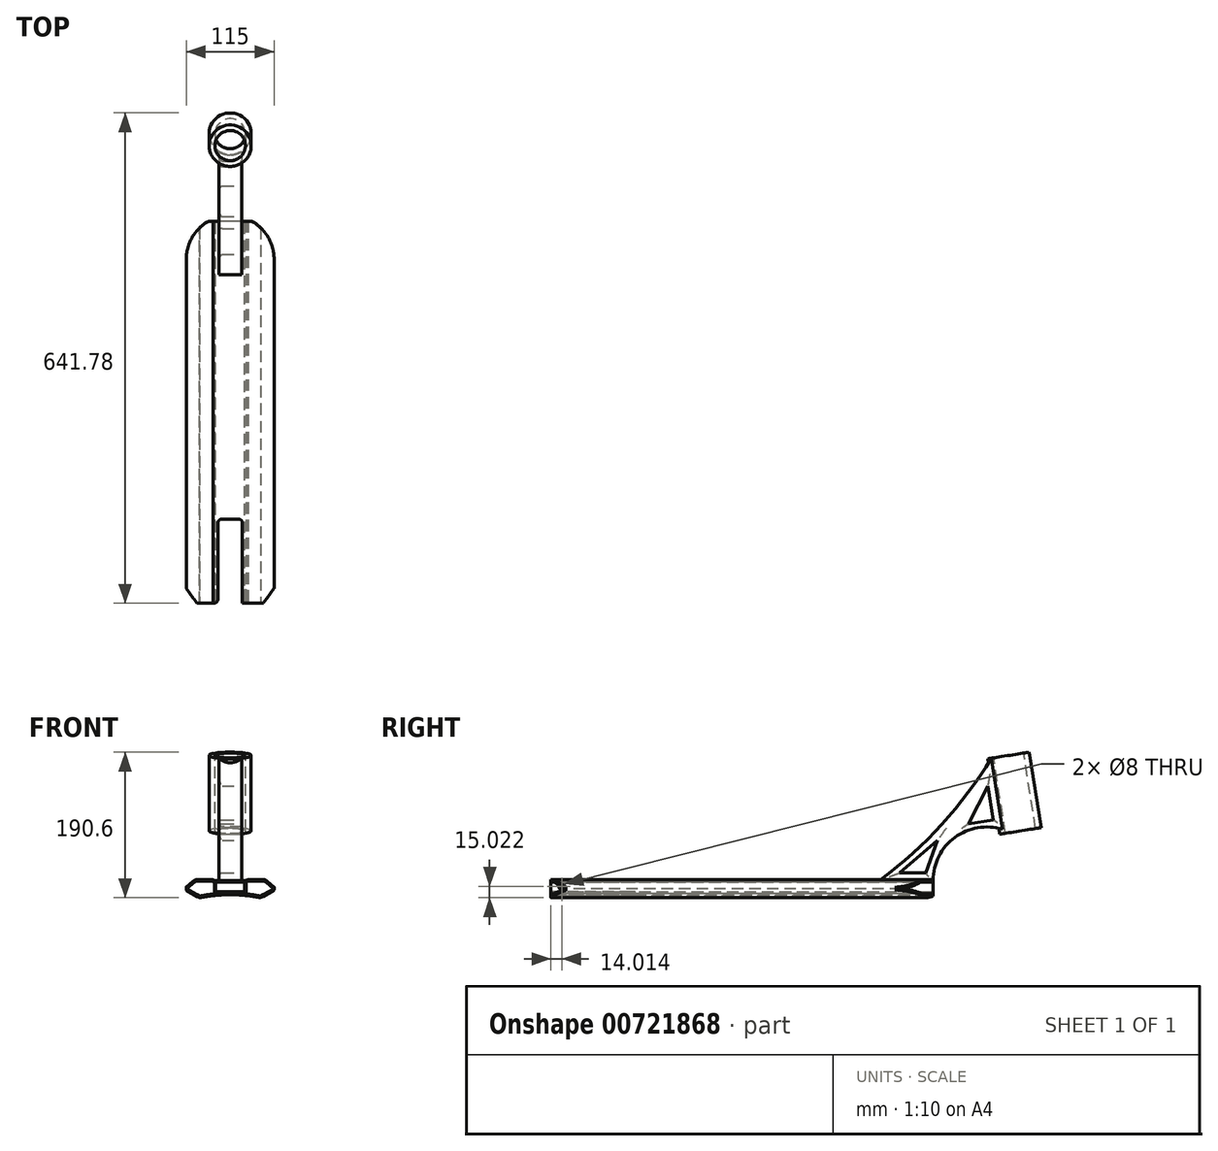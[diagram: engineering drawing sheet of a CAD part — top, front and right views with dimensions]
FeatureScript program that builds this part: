
annotation { "Feature Type Name" : "Feature", "Feature Type Description" : "" }
export const myFeature = defineFeature(function(context is Context, id is Id, definition is map)
    precondition{}
    {
        {
            var Q0;
            Q0=qCreatedBy(makeId("Front.planeOp"),FACE);
            var sketch = newSketch(context, id + "F0", { "sketchPlane" : qUnion([Q0])});
            skLineSegment(sketch, "E0", {"start": v(0, 22.7) * mm, "end": v(22.5, 22.7) * mm});
            skLineSegment(sketch, "E1", {"start": v(22.5, 22.7) * mm, "end": v(22.5, 24) * mm});
            skLineSegment(sketch, "E2", {"start": v(22.5, 24) * mm, "end": v(45.58, 24) * mm});
            skLineSegment(sketch, "E3", {"start": v(45.58, 24) * mm, "end": v(57.5, 14) * mm});
            skLineSegment(sketch, "E4", {"start": v(57.5, 14) * mm, "end": v(57.5, 10) * mm});
            skLineSegment(sketch, "E5", {"start": v(57.5, 10) * mm, "end": v(40.18, 0) * mm});
            skLineSegment(sketch, "E6.MirrorCS", {"start": v(0, 22.7) * mm, "end": v(-22.5, 22.7) * mm});
            skLineSegment(sketch, "E7.MirrorCS", {"start": v(-22.5, 22.7) * mm, "end": v(-22.5, 24) * mm});
            skLineSegment(sketch, "E8.MirrorCS", {"start": v(-22.5, 24) * mm, "end": v(-45.58, 24) * mm});
            skLineSegment(sketch, "E9.MirrorCS", {"start": v(-45.58, 24) * mm, "end": v(-57.5, 14) * mm});
            skLineSegment(sketch, "E10.MirrorCS", {"start": v(-57.5, 14) * mm, "end": v(-57.5, 10) * mm});
            skLineSegment(sketch, "E11.MirrorCS", {"start": v(-57.5, 10) * mm, "end": v(-40.18, 0) * mm});
            skArc(sketch, "E12", {"start": v(40.18, 0) * mm, "mid": v(0, 4.08) * mm, "end": v(-40.18, 0) * mm});
            skSolve(sketch);
        }
        {
            var Q0;
            Q0 = qSketchRegion(id + "F0", true);
            extrude(context, id + "F1", {"entities" : qUnion([Q0]), "endBound" : BoundingType.SYMMETRIC, "depth" : 500 * mm, "offsetDistance" : 25 * mm});
        }
        {
            var Q0;
            Q0=qCreatedBy(makeId("Front.planeOp"),FACE);
            var sketch = newSketch(context, id + "F2", { "sketchPlane" : qUnion([Q0])});
            skLineSegment(sketch, "E13.bottom", {"start": v(19, 7.7) * mm, "end": v(-19, 7.7) * mm});
            skLineSegment(sketch, "E13.top", {"start": v(19, 20.7) * mm, "end": v(-19, 20.7) * mm});
            skLineSegment(sketch, "E13.left", {"start": v(19, 7.7) * mm, "end": v(19, 20.7) * mm});
            skLineSegment(sketch, "E13.right", {"start": v(-19, 7.7) * mm, "end": v(-19, 20.7) * mm});
            skPoint(sketch, "E13.middle", {"position": v(0, 14.2) * mm});
            skSolve(sketch);
        }
        {
            var Q0;
            Q0 = qSketchRegion(id + "F2", true);
            extrude(context, id + "F3", {"entities" : qUnion([Q0]), "operationType" : NewBodyOperationType.REMOVE, "endBound" : BoundingType.SYMMETRIC, "depth" : 500 * mm, "offsetDistance" : 25 * mm});
        }
        {
            var Q0;
            Q0=makeQuery(id+"F1.opExtrude","SWEPT_EDGE",EDGE,{"disambiguationData":[OSD([sQuery(id+"F0.wireOp",EDGE,"E6.MirrorCS"),sQuery(id+"F0.wireOp",EDGE,"E7.MirrorCS")])]});
            var Q1;
            Q1=makeQuery(id+"F1.opExtrude","SWEPT_EDGE",EDGE,{"disambiguationData":[OSD([sQuery(id+"F0.wireOp",EDGE,"E0"),sQuery(id+"F0.wireOp",EDGE,"E1")])]});
            fillet(context, id + "F4", {"entities" : qUnion([Q0, Q1]), "radius" : 2 * mm, "tangentPropagation" : true, "allowEdgeOverflow" : false});
        }
        {
            var Q0;
            Q0=makeQuery(id+"F4.opFillet","BLEND_EDGE",EDGE,{"blendedFrom":[makeQuery(id+"F1.opExtrude","SWEPT_EDGE",EDGE,{"disambiguationData":[OSD([sQuery(id+"F0.wireOp",EDGE,"E0"),sQuery(id+"F0.wireOp",EDGE,"E1")])]}),makeQuery(id+"F1.opExtrude","SWEPT_FACE",FACE,{"disambiguationData":[OSD([sQuery(id+"F0.wireOp",EDGE,"E2")])]})],"blendedInto":[makeQuery(id+"F1.opExtrude","SWEPT_FACE",FACE,{"disambiguationData":[OSD([sQuery(id+"F0.wireOp",EDGE,"E2")])]})]});
            var Q1;
            Q1=makeQuery(id+"F1.opExtrude","SWEPT_EDGE",EDGE,{"disambiguationData":[OSD([sQuery(id+"F0.wireOp",EDGE,"E2"),sQuery(id+"F0.wireOp",EDGE,"E3")])]});
            var Q2;
            Q2=makeQuery(id+"F1.opExtrude","SWEPT_EDGE",EDGE,{"disambiguationData":[OSD([sQuery(id+"F0.wireOp",EDGE,"E8.MirrorCS"),sQuery(id+"F0.wireOp",EDGE,"E9.MirrorCS")])]});
            var Q3;
            Q3=makeQuery(id+"F1.opExtrude","SWEPT_EDGE",EDGE,{"disambiguationData":[OSD([sQuery(id+"F0.wireOp",EDGE,"E5"),sQuery(id+"F0.wireOp",EDGE,"E12")])]});
            fillet(context, id + "F5", {"entities" : qUnion([Q0, Q1, Q2, Q3]), "radius" : 9 * mm, "tangentPropagation" : true, "allowEdgeOverflow" : false});
        }
        {
            var Q0;
            Q0=makeQuery(id+"F1.opExtrude","SWEPT_EDGE",EDGE,{"disambiguationData":[OSD([sQuery(id+"F0.wireOp",EDGE,"E9.MirrorCS"),sQuery(id+"F0.wireOp",EDGE,"E10.MirrorCS")])]});
            var Q1;
            Q1=makeQuery(id+"F1.opExtrude","SWEPT_EDGE",EDGE,{"disambiguationData":[OSD([sQuery(id+"F0.wireOp",EDGE,"E10.MirrorCS"),sQuery(id+"F0.wireOp",EDGE,"E11.MirrorCS")])]});
            var Q2;
            Q2=makeQuery(id+"F1.opExtrude","SWEPT_EDGE",EDGE,{"disambiguationData":[OSD([sQuery(id+"F0.wireOp",EDGE,"E3"),sQuery(id+"F0.wireOp",EDGE,"E4")])]});
            var Q3;
            Q3=makeQuery(id+"F1.opExtrude","SWEPT_EDGE",EDGE,{"disambiguationData":[OSD([sQuery(id+"F0.wireOp",EDGE,"E4"),sQuery(id+"F0.wireOp",EDGE,"E5")])]});
            fillet(context, id + "F6", {"entities" : qUnion([Q0, Q1, Q2, Q3]), "radius" : 1 * mm, "tangentPropagation" : true, "allowEdgeOverflow" : false});
        }
        {
            var Q0;
            Q0=makeQuery(id+"F1.opExtrude","CAP_FACE",FACE,{"disambiguationData":[OSD([sQuery(id+"F0.wireOp",EDGE,"E0"),sQuery(id+"F0.wireOp",EDGE,"E1"),sQuery(id+"F0.wireOp",EDGE,"E2"),sQuery(id+"F0.wireOp",EDGE,"E3"),sQuery(id+"F0.wireOp",EDGE,"E4"),sQuery(id+"F0.wireOp",EDGE,"E5"),sQuery(id+"F0.wireOp",EDGE,"E6.MirrorCS"),sQuery(id+"F0.wireOp",EDGE,"E7.MirrorCS"),sQuery(id+"F0.wireOp",EDGE,"E8.MirrorCS"),sQuery(id+"F0.wireOp",EDGE,"E9.MirrorCS"),sQuery(id+"F0.wireOp",EDGE,"E10.MirrorCS"),sQuery(id+"F0.wireOp",EDGE,"E11.MirrorCS"),sQuery(id+"F0.wireOp",EDGE,"E12")])],"isStart":false});
            var sketch = newSketch(context, id + "F7", { "sketchPlane" : qUnion([Q0])});
            skArc(sketch, "E14.0", {"start": v(37.3, 2.6) * mm, "mid": v(-1.29, 6.07) * mm, "end": v(-39.84, 2.11) * mm});
            skLineSegment(sketch, "E14.1", {"start": v(-56.85, 11.93) * mm, "end": v(-39.84, 2.11) * mm});
            skArc(sketch, "E14.2", {"start": v(-20.63, 20.7) * mm, "mid": v(-22.24, 21.04) * mm, "end": v(-23.58, 22) * mm});
            skLineSegment(sketch, "E14.3", {"start": v(-23.58, 22) * mm, "end": v(-42.3, 22) * mm});
            skArc(sketch, "E14.4", {"start": v(-42.3, 22) * mm, "mid": v(-44.7, 21.58) * mm, "end": v(-46.8, 20.36) * mm});
            skLineSegment(sketch, "E14.5", {"start": v(-46.8, 20.36) * mm, "end": v(-56.85, 11.93) * mm});
            skLineSegment(sketch, "E15", {"start": v(-20.63, 20.7) * mm, "end": v(-20.63, 5.02) * mm});
            skLineSegment(sketch, "E16.MirrorCS", {"start": v(23.58, 22) * mm, "end": v(42.3, 22) * mm});
            skArc(sketch, "E17.MirrorCS", {"start": v(42.3, 22) * mm, "mid": v(44.7, 21.58) * mm, "end": v(46.8, 20.36) * mm});
            skLineSegment(sketch, "E18.MirrorCS", {"start": v(46.8, 20.36) * mm, "end": v(56.85, 11.93) * mm});
            skLineSegment(sketch, "E19.MirrorCS", {"start": v(56.85, 11.93) * mm, "end": v(39.84, 2.11) * mm});
            skArc(sketch, "E20.MirrorCS", {"start": v(-37.3, 2.6) * mm, "mid": v(1.29, 6.07) * mm, "end": v(39.84, 2.11) * mm});
            skLineSegment(sketch, "E21.MirrorCS", {"start": v(20.63, 20.7) * mm, "end": v(20.63, 5.02) * mm});
            skArc(sketch, "E22.MirrorCS", {"start": v(20.63, 20.7) * mm, "mid": v(22.24, 21.04) * mm, "end": v(23.58, 22) * mm});
            skSolve(sketch);
        }
        {
            var Q0;
            {var subQ0=sQuery(id+"F7.wireOp",EDGE,"E14.0");Q0=makeQuery(id+"F7.imprint","IMPRINT",FACE,{"disambiguationData":[TD([[makeQuery(id+"F7.imprint","IMPRINT",EDGE,{"derivedFrom":subQ0}),-1.0]])]});}
            var Q1;
            Q1=makeQuery(id+"F7.imprint","IMPRINT",FACE,{"disambiguationData":[TD([[makeQuery(id+"F7.imprint","IMPRINT",EDGE,{"derivedFrom":sQuery(id+"F7.wireOp",EDGE,"E16.MirrorCS")}),-1.0]])]});
            extrude(context, id + "F8", {"entities" : qUnion([Q0, Q1]), "operationType" : NewBodyOperationType.REMOVE, "endBound" : BoundingType.THROUGH_ALL, "oppositeDirection" : true, "depth" : 25 * mm, "offsetDistance" : 25 * mm});
        }
        {
            var Q0;
            Q0=qCreatedBy(makeId("Top.planeOp"),FACE);
            var sketch = newSketch(context, id + "F9", { "sketchPlane" : qUnion([Q0])});
            skArc(sketch, "E23", {"start": v(57.5, 200) * mm, "mid": v(0, 257.5) * mm, "end": v(-57.5, 200) * mm});
            skLineSegment(sketch, "E24", {"start": v(57.5, 200) * mm, "end": v(57.5, 280) * mm});
            skLineSegment(sketch, "E25", {"start": v(57.5, 280) * mm, "end": v(-57.5, 280) * mm});
            skLineSegment(sketch, "E26", {"start": v(-57.5, 280) * mm, "end": v(-57.5, 200) * mm});
            skSolve(sketch);
        }
        {
            var Q0;
            Q0=makeQuery(id+"F9.imprint","IMPRINT",FACE,{"disambiguationData":[TD([[makeQuery(id+"F9.imprint","IMPRINT",EDGE,{"derivedFrom":sQuery(id+"F9.wireOp",EDGE,"E23")}),-1.0]])]});
            extrude(context, id + "F10", {"entities" : qUnion([Q0]), "operationType" : NewBodyOperationType.REMOVE, "endBound" : BoundingType.THROUGH_ALL, "oppositeDirection" : true, "depth" : 25 * mm, "offsetDistance" : 25 * mm, "hasSecondDirection" : true, "secondDirectionBound" : SecondDirectionBoundingType.THROUGH_ALL, "secondDirectionOppositeDirection" : false, "secondDirectionDepth" : 25 * mm});
        }
        {
            var Q0;
            Q0=qCreatedBy(makeId("Top.planeOp"),FACE);
            var sketch = newSketch(context, id + "F11", { "sketchPlane" : qUnion([Q0])});
            skLineSegment(sketch, "E27", {"start": v(43.28, -250.03) * mm, "end": v(68, -216) * mm});
            skLineSegment(sketch, "E28", {"start": v(68, -216) * mm, "end": v(68, -346) * mm});
            skLineSegment(sketch, "E29", {"start": v(-68, -346) * mm, "end": v(-68, -216) * mm});
            skLineSegment(sketch, "E30", {"start": v(-68, -216) * mm, "end": v(-43.32, -249.97) * mm});
            skLineSegment(sketch, "E31", {"start": v(-16.12, -249.97) * mm, "end": v(-16, -139.97) * mm});
            skPoint(sketch, "E32.orphan", {"position": v(101.08, -377.14) * mm});
            skPoint(sketch, "E33.start.orphan", {"position": v(62.55, -216) * mm});
            skLineSegment(sketch, "E34", {"start": v(16, -140) * mm, "end": v(16, -250) * mm});
            skLineSegment(sketch, "E35", {"start": v(16, -250) * mm, "end": v(43.28, -250.03) * mm});
            skLineSegment(sketch, "E36", {"start": v(-16.12, -249.97) * mm, "end": v(-43.32, -249.97) * mm});
            skPoint(sketch, "E37.orphan", {"position": v(49.07, -377.14) * mm});
            skPoint(sketch, "E38.start.orphan", {"position": v(0, -346) * mm});
            skLineSegment(sketch, "E39", {"start": v(-68.33, -345.04) * mm, "end": v(68, -346) * mm});
            skPoint(sketch, "E40.start.orphan", {"position": v(0, -139.98) * mm});
            skLineSegment(sketch, "E41", {"start": v(-16, -139.97) * mm, "end": v(16, -140) * mm});
            skSolve(sketch);
        }
        {
            var Q0;
            Q0=makeQuery(id+"F11.imprint","IMPRINT",FACE,{"disambiguationData":[TD([[makeQuery(id+"F11.imprint","IMPRINT",EDGE,{"derivedFrom":sQuery(id+"F11.wireOp",EDGE,"E27")}),-1.0]])]});
            extrude(context, id + "F12", {"entities" : qUnion([Q0]), "operationType" : NewBodyOperationType.REMOVE, "endBound" : BoundingType.THROUGH_ALL, "depth" : 25 * mm, "offsetDistance" : 25 * mm, "hasSecondDirection" : true, "secondDirectionBound" : SecondDirectionBoundingType.THROUGH_ALL, "secondDirectionOppositeDirection" : true, "secondDirectionDepth" : 25 * mm});
        }
        {
            var Q0;
            {var subQ0=sQuery(id+"F11.wireOp",EDGE,"E31");var subQ1=sQuery(id+"F11.wireOp",EDGE,"E41");Q0=makeQuery(id+"F12.boolean.opBoolean","COPY",EDGE,{"disambiguationData":[TD([makeQuery(id+"F3.boolean.opBoolean","COPY",FACE,{"derivedFrom":makeQuery(id+"F3.opExtrude","SWEPT_FACE",FACE,{"disambiguationData":[OSD([sQuery(id+"F2.wireOp",EDGE,"E13.top")])]})})])],"derivedFrom":makeQuery(id+"F12.opExtrude","SWEPT_EDGE",EDGE,{"disambiguationData":[OSD([subQ0,subQ1])]})});}
            var Q1;
            {var subQ0=sQuery(id+"F11.wireOp",EDGE,"E31");var subQ1=sQuery(id+"F11.wireOp",EDGE,"E41");Q1=makeQuery(id+"F12.boolean.opBoolean","COPY",EDGE,{"disambiguationData":[TD([makeQuery(id+"F1.opExtrude","SWEPT_FACE",FACE,{"disambiguationData":[OSD([sQuery(id+"F0.wireOp",EDGE,"E12")])]})])],"derivedFrom":makeQuery(id+"F12.opExtrude","SWEPT_EDGE",EDGE,{"disambiguationData":[OSD([subQ0,subQ1])]})});}
            var Q2;
            {var subQ0=sQuery(id+"F11.wireOp",EDGE,"E41");var subQ1=sQuery(id+"F11.wireOp",EDGE,"E34");Q2=makeQuery(id+"F12.boolean.opBoolean","COPY",EDGE,{"disambiguationData":[TD([makeQuery(id+"F3.boolean.opBoolean","COPY",FACE,{"derivedFrom":makeQuery(id+"F3.opExtrude","SWEPT_FACE",FACE,{"disambiguationData":[OSD([sQuery(id+"F2.wireOp",EDGE,"E13.top")])]})})])],"derivedFrom":makeQuery(id+"F12.opExtrude","SWEPT_EDGE",EDGE,{"disambiguationData":[OSD([subQ1,subQ0])]})});}
            var Q3;
            {var subQ0=sQuery(id+"F11.wireOp",EDGE,"E34");var subQ1=sQuery(id+"F11.wireOp",EDGE,"E41");Q3=makeQuery(id+"F12.boolean.opBoolean","COPY",EDGE,{"disambiguationData":[TD([makeQuery(id+"F1.opExtrude","SWEPT_FACE",FACE,{"disambiguationData":[OSD([sQuery(id+"F0.wireOp",EDGE,"E12")])]})])],"derivedFrom":makeQuery(id+"F12.opExtrude","SWEPT_EDGE",EDGE,{"disambiguationData":[OSD([subQ0,subQ1])]})});}
            var Q4;
            {var subQ0=sQuery(id+"F11.wireOp",EDGE,"E31");var subQ1=sQuery(id+"F11.wireOp",EDGE,"E36");Q4=makeQuery(id+"F12.boolean.opBoolean","COPY",EDGE,{"disambiguationData":[TD([makeQuery(id+"F3.boolean.opBoolean","COPY",FACE,{"derivedFrom":makeQuery(id+"F3.opExtrude","SWEPT_FACE",FACE,{"disambiguationData":[OSD([sQuery(id+"F2.wireOp",EDGE,"E13.top")])]})})])],"derivedFrom":makeQuery(id+"F12.opExtrude","SWEPT_EDGE",EDGE,{"disambiguationData":[OSD([subQ0,subQ1])]})});}
            var Q5;
            {var subQ2=sQuery(id+"F11.wireOp",EDGE,"E34");Q5=makeQuery(id+"F12.boolean.opBoolean","COPY",EDGE,{"disambiguationData":[TD([makeQuery(id+"F3.boolean.opBoolean","COPY",FACE,{"derivedFrom":makeQuery(id+"F3.opExtrude","SWEPT_FACE",FACE,{"disambiguationData":[OSD([sQuery(id+"F2.wireOp",EDGE,"E13.top")])]})})])],"derivedFrom":makeQuery(id+"F12.opExtrude","SWEPT_EDGE",EDGE,{"disambiguationData":[OSD([subQ2,sQuery(id+"F11.wireOp",EDGE,"E35")])]})});}
            fillet(context, id + "F13", {"entities" : qUnion([Q0, Q1, Q2, Q3, Q4, Q5]), "radius" : 5 * mm, "tangentPropagation" : true, "allowEdgeOverflow" : false});
        }
        {
            var Q0;
            Q0=qCreatedBy(makeId("Right.planeOp"),FACE);
            var sketch = newSketch(context, id + "F14", { "sketchPlane" : qUnion([Q0])});
            skLineSegment(sketch, "E42", {"start": v(180, 22.7) * mm, "end": v(250, 22.7) * mm});
            skLineSegment(sketch, "E43", {"start": v(341.9, 83.93) * mm, "end": v(387.33, 91.13) * mm});
            skLineSegment(sketch, "E44", {"start": v(387.33, 91.13) * mm, "end": v(371.69, 189.9) * mm});
            skLineSegment(sketch, "E45", {"start": v(371.69, 189.9) * mm, "end": v(326.25, 182.7) * mm});
            skPoint(sketch, "E46.end.orphan", {"position": v(250, 75.32) * mm});
            skPoint(sketch, "E47.orphan", {"position": v(371.69, 51.7) * mm});
            skPoint(sketch, "E48.orphan", {"position": v(307.98, 78.56) * mm});
            skArc(sketch, "E49", {"start": v(180, 22.7) * mm, "mid": v(261.09, 95.42) * mm, "end": v(326.25, 182.7) * mm});
            skPoint(sketch, "E50.center.orphan", {"position": v(307.98, 22.7) * mm});
            skLineSegment(sketch, "E51", {"start": v(341.9, 83.93) * mm, "end": v(341.02, 89.47) * mm});
            skArc(sketch, "E52", {"start": v(341.02, 89.47) * mm, "mid": v(278.6, 79.14) * mm, "end": v(250, 22.7) * mm});
            skSolve(sketch);
        }
        {
            var Q0;
            Q0 = qSketchRegion(id + "F14", true);
            extrude(context, id + "F15", {"entities" : qUnion([Q0]), "operationType" : NewBodyOperationType.ADD, "endBound" : BoundingType.SYMMETRIC, "depth" : 30 * mm, "offsetDistance" : 25 * mm});
        }
        {
            var Q0;
            Q0=makeQuery(id+"F15.opExtrude","SWEPT_FACE",FACE,{"disambiguationData":[OSD([sQuery(id+"F14.wireOp",EDGE,"E45")])]});
            var sketch = newSketch(context, id + "F16", { "sketchPlane" : qUnion([Q0])});
            skCircle(sketch, "E53", {"center": v(0, 373.82) * mm, "radius": 27.5 * mm});
            skSolve(sketch);
        }
        {
            var Q0;
            Q0 = qSketchRegion(id + "F16", true);
            extrude(context, id + "F17", {"entities" : qUnion([Q0]), "operationType" : NewBodyOperationType.ADD, "oppositeDirection" : true, "depth" : 100 * mm, "offsetDistance" : 25 * mm});
        }
        {
            var Q0;
            Q0=makeQuery(id+"F17.boolean.opBoolean","MERGE",FACE,{"derivedFrom":[makeQuery(id+"F15.opExtrude","SWEPT_FACE",FACE,{"disambiguationData":[OSD([sQuery(id+"F14.wireOp",EDGE,"E45")])]}),makeQuery(id+"F17.opExtrude","CAP_FACE",FACE,{"disambiguationData":[OSD([sQuery(id+"F16.wireOp",EDGE,"E53")])],"isStart":true})]});
            var sketch = newSketch(context, id + "F18", { "sketchPlane" : qUnion([Q0])});
            skPoint(sketch, "E54", {"position": v(0, 373.82) * mm});
            skSolve(sketch);
        }
        {
            var Q0;
            Q0=sQuery(id+"F18.wireOp",VERTEX,"E54");
            var Q1;
            Q1=makeQuery(id+"F1.opExtrude","SWEPT_BODY",BODY,{"disambiguationData":[OSD([sQuery(id+"F0.wireOp",EDGE,"E0"),sQuery(id+"F0.wireOp",EDGE,"E1"),sQuery(id+"F0.wireOp",EDGE,"E2"),sQuery(id+"F0.wireOp",EDGE,"E3"),sQuery(id+"F0.wireOp",EDGE,"E4"),sQuery(id+"F0.wireOp",EDGE,"E5"),sQuery(id+"F0.wireOp",EDGE,"E6.MirrorCS"),sQuery(id+"F0.wireOp",EDGE,"E7.MirrorCS"),sQuery(id+"F0.wireOp",EDGE,"E8.MirrorCS"),sQuery(id+"F0.wireOp",EDGE,"E9.MirrorCS"),sQuery(id+"F0.wireOp",EDGE,"E10.MirrorCS"),sQuery(id+"F0.wireOp",EDGE,"E11.MirrorCS"),sQuery(id+"F0.wireOp",EDGE,"E12")])]});
            hole(context, id + "F19", {"style" : HoleStyle.SIMPLE, "endStyle" : HoleEndStyle.THROUGH, "holeDiameter" : 40 * mm, "majorDiameter" : 5 * mm, "isTappedThrough" : true, "tappedDepth" : 12 * mm, "tapClearance" : 3, "locations" : qUnion([Q0]), "scope" : qUnion([Q1])});
        }
        {
            var Q0;
            Q0=makeQuery(id+"F8.boolean.opBoolean","COPY",FACE,{"derivedFrom":makeQuery(id+"F8.opExtrude","SWEPT_FACE",FACE,{"disambiguationData":[OSD([sQuery(id+"F7.wireOp",EDGE,"E21.MirrorCS")])]})});
            var sketch = newSketch(context, id + "F20", { "sketchPlane" : qUnion([Q0])});
            skPoint(sketch, "E55", {"position": v(-235.99, 15.02) * mm});
            skSolve(sketch);
        }
        {
            var Q0;
            Q0=sQuery(id+"F20.wireOp",VERTEX,"E55");
            var Q1;
            Q1=makeQuery(id+"F1.opExtrude","SWEPT_BODY",BODY,{"disambiguationData":[OSD([sQuery(id+"F0.wireOp",EDGE,"E0"),sQuery(id+"F0.wireOp",EDGE,"E1"),sQuery(id+"F0.wireOp",EDGE,"E2"),sQuery(id+"F0.wireOp",EDGE,"E3"),sQuery(id+"F0.wireOp",EDGE,"E4"),sQuery(id+"F0.wireOp",EDGE,"E5"),sQuery(id+"F0.wireOp",EDGE,"E6.MirrorCS"),sQuery(id+"F0.wireOp",EDGE,"E7.MirrorCS"),sQuery(id+"F0.wireOp",EDGE,"E8.MirrorCS"),sQuery(id+"F0.wireOp",EDGE,"E9.MirrorCS"),sQuery(id+"F0.wireOp",EDGE,"E10.MirrorCS"),sQuery(id+"F0.wireOp",EDGE,"E11.MirrorCS"),sQuery(id+"F0.wireOp",EDGE,"E12")])]});
            hole(context, id + "F21", {"style" : HoleStyle.SIMPLE, "endStyle" : HoleEndStyle.BLIND, "holeDiameter" : 8 * mm, "majorDiameter" : 5 * mm, "holeDepth" : 50 * mm, "isTappedThrough" : true, "tappedDepth" : 12 * mm, "tapClearance" : 3, "locations" : qUnion([Q0]), "scope" : qUnion([Q1])});
        }
        {
            var Q0;
            Q0=makeQuery(id+"F15.opExtrude","CAP_FACE",FACE,{"disambiguationData":[OSD([sQuery(id+"F14.wireOp",EDGE,"E42"),sQuery(id+"F14.wireOp",EDGE,"E43"),sQuery(id+"F14.wireOp",EDGE,"E44"),sQuery(id+"F14.wireOp",EDGE,"E45"),sQuery(id+"F14.wireOp",EDGE,"E49"),sQuery(id+"F14.wireOp",EDGE,"E51"),sQuery(id+"F14.wireOp",EDGE,"E52")])],"isStart":false});
            var sketch = newSketch(context, id + "F22", { "sketchPlane" : qUnion([Q0])});
            skLineSegment(sketch, "E56", {"start": v(296.25, 96.95) * mm, "end": v(328.84, 102.11) * mm});
            skLineSegment(sketch, "E57", {"start": v(328.84, 102.11) * mm, "end": v(321.8, 146.56) * mm});
            skLineSegment(sketch, "E58", {"start": v(321.8, 146.56) * mm, "end": v(296.25, 96.95) * mm});
            skLineSegment(sketch, "E59", {"start": v(240.63, 32.7) * mm, "end": v(206.63, 32.7) * mm});
            skLineSegment(sketch, "E60", {"start": v(240.63, 32.7) * mm, "end": v(256.02, 74.99) * mm});
            skLineSegment(sketch, "E61", {"start": v(256.02, 74.99) * mm, "end": v(206.63, 32.7) * mm});
            skSolve(sketch);
        }
        {
            var Q0;
            Q0 = qSketchRegion(id + "F22", true);
            extrude(context, id + "F23", {"entities" : qUnion([Q0]), "operationType" : NewBodyOperationType.REMOVE, "endBound" : BoundingType.THROUGH_ALL, "oppositeDirection" : true, "depth" : 25 * mm, "offsetDistance" : 25 * mm});
        }
        {
            var Q0;
            Q0=makeQuery(id+"F23.boolean.opBoolean","COPY",EDGE,{"derivedFrom":makeQuery(id+"F23.opExtrude","CAP_EDGE",EDGE,{"disambiguationData":[OSD([sQuery(id+"F22.wireOp",EDGE,"E61")])],"isStart":true})});
            var Q1;
            Q1=makeQuery(id+"F23.boolean.opBoolean","COPY",EDGE,{"derivedFrom":makeQuery(id+"F23.opExtrude","CAP_EDGE",EDGE,{"disambiguationData":[OSD([sQuery(id+"F22.wireOp",EDGE,"E59")])],"isStart":true})});
            var Q2;
            Q2=makeQuery(id+"F23.boolean.opBoolean","COPY",EDGE,{"derivedFrom":makeQuery(id+"F23.opExtrude","CAP_EDGE",EDGE,{"disambiguationData":[OSD([sQuery(id+"F22.wireOp",EDGE,"E60")])],"isStart":true})});
            var Q3;
            Q3=makeQuery(id+"F23.boolean.opBoolean","INTERSECT",EDGE,{"derivedFrom":[makeQuery(id+"F15.opExtrude","CAP_FACE",FACE,{"disambiguationData":[OSD([sQuery(id+"F14.wireOp",EDGE,"E42"),sQuery(id+"F14.wireOp",EDGE,"E43"),sQuery(id+"F14.wireOp",EDGE,"E44"),sQuery(id+"F14.wireOp",EDGE,"E45"),sQuery(id+"F14.wireOp",EDGE,"E49"),sQuery(id+"F14.wireOp",EDGE,"E51"),sQuery(id+"F14.wireOp",EDGE,"E52")])],"isStart":true}),makeQuery(id+"F23.opExtrude","SWEPT_FACE",FACE,{"disambiguationData":[OSD([sQuery(id+"F22.wireOp",EDGE,"E60")])]})]});
            var Q4;
            Q4=makeQuery(id+"F23.boolean.opBoolean","INTERSECT",EDGE,{"derivedFrom":[makeQuery(id+"F15.opExtrude","CAP_FACE",FACE,{"disambiguationData":[OSD([sQuery(id+"F14.wireOp",EDGE,"E42"),sQuery(id+"F14.wireOp",EDGE,"E43"),sQuery(id+"F14.wireOp",EDGE,"E44"),sQuery(id+"F14.wireOp",EDGE,"E45"),sQuery(id+"F14.wireOp",EDGE,"E49"),sQuery(id+"F14.wireOp",EDGE,"E51"),sQuery(id+"F14.wireOp",EDGE,"E52")])],"isStart":true}),makeQuery(id+"F23.opExtrude","SWEPT_FACE",FACE,{"disambiguationData":[OSD([sQuery(id+"F22.wireOp",EDGE,"E61")])]})]});
            var Q5;
            Q5=makeQuery(id+"F23.boolean.opBoolean","INTERSECT",EDGE,{"derivedFrom":[makeQuery(id+"F15.opExtrude","CAP_FACE",FACE,{"disambiguationData":[OSD([sQuery(id+"F14.wireOp",EDGE,"E42"),sQuery(id+"F14.wireOp",EDGE,"E43"),sQuery(id+"F14.wireOp",EDGE,"E44"),sQuery(id+"F14.wireOp",EDGE,"E45"),sQuery(id+"F14.wireOp",EDGE,"E49"),sQuery(id+"F14.wireOp",EDGE,"E51"),sQuery(id+"F14.wireOp",EDGE,"E52")])],"isStart":true}),makeQuery(id+"F23.opExtrude","SWEPT_FACE",FACE,{"disambiguationData":[OSD([sQuery(id+"F22.wireOp",EDGE,"E59")])]})]});
            var Q6;
            Q6=makeQuery(id+"F23.boolean.opBoolean","INTERSECT",EDGE,{"derivedFrom":[makeQuery(id+"F15.opExtrude","CAP_FACE",FACE,{"disambiguationData":[OSD([sQuery(id+"F14.wireOp",EDGE,"E42"),sQuery(id+"F14.wireOp",EDGE,"E43"),sQuery(id+"F14.wireOp",EDGE,"E44"),sQuery(id+"F14.wireOp",EDGE,"E45"),sQuery(id+"F14.wireOp",EDGE,"E49"),sQuery(id+"F14.wireOp",EDGE,"E51"),sQuery(id+"F14.wireOp",EDGE,"E52")])],"isStart":true}),makeQuery(id+"F23.opExtrude","SWEPT_FACE",FACE,{"disambiguationData":[OSD([sQuery(id+"F22.wireOp",EDGE,"E56")])]})]});
            var Q7;
            Q7=makeQuery(id+"F23.boolean.opBoolean","COPY",EDGE,{"derivedFrom":makeQuery(id+"F23.opExtrude","CAP_EDGE",EDGE,{"disambiguationData":[OSD([sQuery(id+"F22.wireOp",EDGE,"E56")])],"isStart":true})});
            var Q8;
            Q8=makeQuery(id+"F23.boolean.opBoolean","INTERSECT",EDGE,{"derivedFrom":[makeQuery(id+"F15.opExtrude","CAP_FACE",FACE,{"disambiguationData":[OSD([sQuery(id+"F14.wireOp",EDGE,"E42"),sQuery(id+"F14.wireOp",EDGE,"E43"),sQuery(id+"F14.wireOp",EDGE,"E44"),sQuery(id+"F14.wireOp",EDGE,"E45"),sQuery(id+"F14.wireOp",EDGE,"E49"),sQuery(id+"F14.wireOp",EDGE,"E51"),sQuery(id+"F14.wireOp",EDGE,"E52")])],"isStart":true}),makeQuery(id+"F23.opExtrude","SWEPT_FACE",FACE,{"disambiguationData":[OSD([sQuery(id+"F22.wireOp",EDGE,"E57")])]})]});
            var Q9;
            Q9=makeQuery(id+"F23.boolean.opBoolean","INTERSECT",EDGE,{"derivedFrom":[makeQuery(id+"F15.opExtrude","CAP_FACE",FACE,{"disambiguationData":[OSD([sQuery(id+"F14.wireOp",EDGE,"E42"),sQuery(id+"F14.wireOp",EDGE,"E43"),sQuery(id+"F14.wireOp",EDGE,"E44"),sQuery(id+"F14.wireOp",EDGE,"E45"),sQuery(id+"F14.wireOp",EDGE,"E49"),sQuery(id+"F14.wireOp",EDGE,"E51"),sQuery(id+"F14.wireOp",EDGE,"E52")])],"isStart":true}),makeQuery(id+"F23.opExtrude","SWEPT_FACE",FACE,{"disambiguationData":[OSD([sQuery(id+"F22.wireOp",EDGE,"E58")])]})]});
            var Q10;
            Q10=makeQuery(id+"F23.boolean.opBoolean","COPY",EDGE,{"derivedFrom":makeQuery(id+"F23.opExtrude","CAP_EDGE",EDGE,{"disambiguationData":[OSD([sQuery(id+"F22.wireOp",EDGE,"E58")])],"isStart":true})});
            var Q11;
            Q11=makeQuery(id+"F23.boolean.opBoolean","COPY",EDGE,{"derivedFrom":makeQuery(id+"F23.opExtrude","CAP_EDGE",EDGE,{"disambiguationData":[OSD([sQuery(id+"F22.wireOp",EDGE,"E57")])],"isStart":true})});
            fillet(context, id + "F24", {"entities" : qUnion([Q0, Q1, Q2, Q3, Q4, Q5, Q6, Q7, Q8, Q9, Q10, Q11]), "radius" : 5 * mm, "tangentPropagation" : true, "allowEdgeOverflow" : false});
        }
    });
